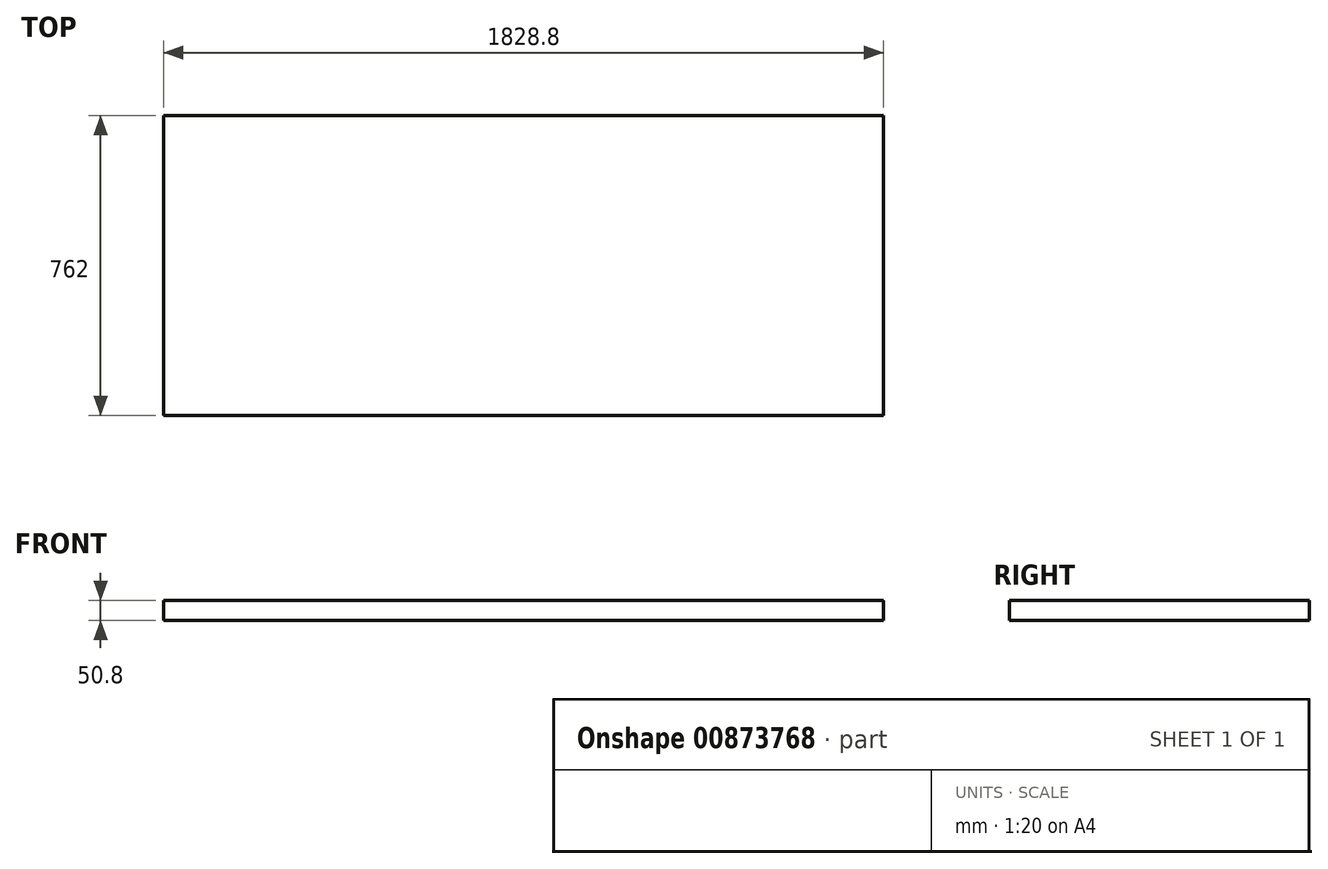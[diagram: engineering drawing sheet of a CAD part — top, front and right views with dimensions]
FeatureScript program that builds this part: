
annotation { "Feature Type Name" : "Feature", "Feature Type Description" : "" }
export const myFeature = defineFeature(function(context is Context, id is Id, definition is map)
    precondition{}
    {
        {
            var Q0;
            Q0=qCreatedBy(makeId("Top.planeOp"),FACE);
            var sketch = newSketch(context, id + "F0", { "sketchPlane" : qUnion([Q0])});
            skLineSegment(sketch, "E0.bottom", {"start": v(0, 0) * mm, "end": v(1828.8, 0) * mm});
            skLineSegment(sketch, "E0.top", {"start": v(0, 762) * mm, "end": v(1828.8, 762) * mm});
            skLineSegment(sketch, "E0.left", {"start": v(0, 0) * mm, "end": v(0, 762) * mm});
            skLineSegment(sketch, "E0.right", {"start": v(1828.8, 0) * mm, "end": v(1828.8, 762) * mm});
            skSolve(sketch);
        }
        {
            var Q0;
            Q0 = qSketchRegion(id + "F0", true);
            extrude(context, id + "F1", {"entities" : qUnion([Q0]), "depth" : 50.8 * mm, "offsetDistance" : 25.4 * mm});
        }
    });
